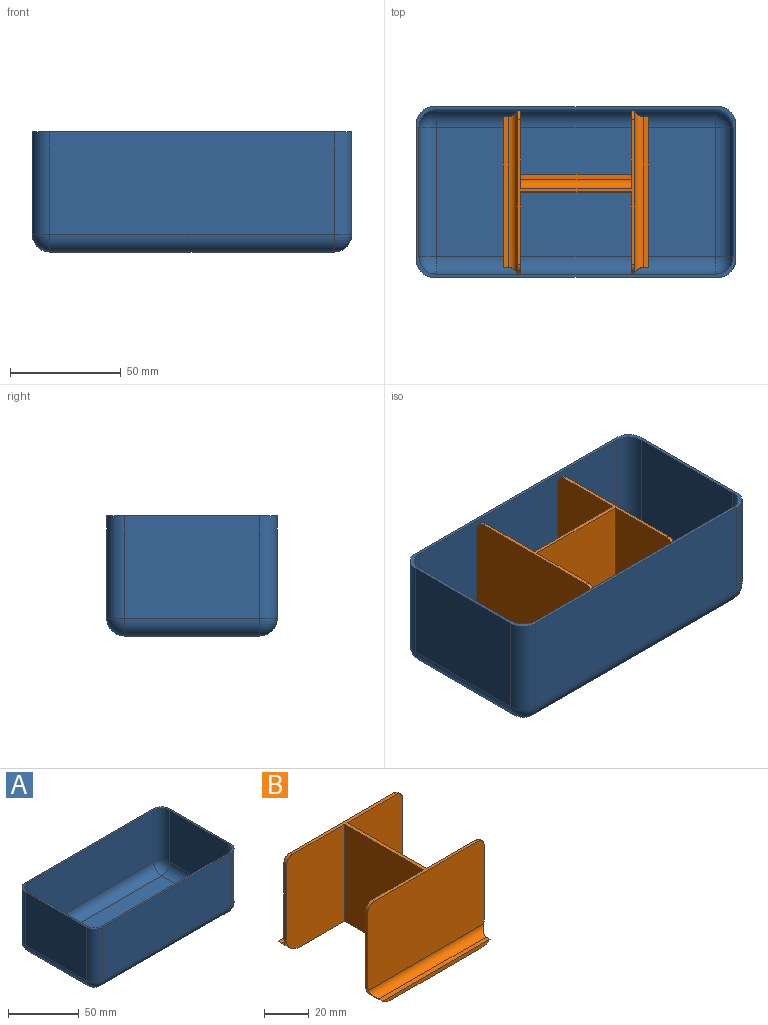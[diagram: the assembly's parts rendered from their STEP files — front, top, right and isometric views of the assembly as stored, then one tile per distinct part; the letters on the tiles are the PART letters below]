
ASSEMBLY  parts=2 mates=1
PART A: 35 faces, bbox 144.6x77.1x54.3 mm
  f0: plane 61.1x46.3mm, normal (1,0,0), area 2828.9mm2, adj f8,f13,f16,f26
  f1: plane 128.6x46.3mm, normal (0,1,0), area 5954.2mm2, adj f8,f13,f14,f22
  f2: plane 61.1x46.3mm, normal (-1,0,0), area 2828.9mm2, adj f8,f14,f15,f19
  f3: plane 58.5x45mm, normal (1,0,0), area 2632.5mm2, adj f8,f9,f12,f32
  f4: plane 126x45mm, normal (0,-1,0), area 5670mm2, adj f8,f9,f10,f28
  f5: plane 58.5x45mm, normal (-1,0,0), area 2632.5mm2, adj f8,f10,f11,f29
  f6: plane 126x45mm, normal (0,1,0), area 5670mm2, adj f8,f11,f12,f33
  f7: plane 128.6x46.3mm, normal (0,-1,0), area 5954.2mm2, adj f8,f15,f16,f23
  f8: plane 144.6x77.1mm, normal (0,0,1), area 569.7mm2, adj f0,f1,f2,f3,f4,f5,f6,f7
  f9: cylinder r=8mm len=45mm, axis (0,0,-1), area 565.5mm2, adj f3,f4,f8,f30
  f10: cylinder r=8mm len=45mm, axis (0,0,1), area 565.5mm2, adj f4,f5,f8,f27
  f11: cylinder r=8mm len=45mm, axis (0,0,-1), area 565.5mm2, adj f5,f6,f8,f31
  f12: cylinder r=8mm len=45mm, axis (0,0,1), area 565.5mm2, adj f3,f6,f8,f34
  f13: cylinder r=8mm len=46.3mm, axis (0,0,-1), area 581.8mm2, adj f0,f1,f8,f24
  f14: cylinder r=8mm len=46.3mm, axis (0,0,1), area 581.8mm2, adj f1,f2,f8,f20
  f15: cylinder r=8mm len=46.3mm, axis (0,0,-1), area 581.8mm2, adj f2,f7,f8,f21
  f16: cylinder r=8mm len=46.3mm, axis (0,0,1), area 581.8mm2, adj f0,f7,f8,f25
  f17: plane 126x58.5mm, normal (0,0,1), area 7371mm2, adj f28,f29,f32,f33
  f18: plane 128.6x61.1mm, normal (0,0,-1), area 7857.5mm2, adj f19,f22,f23,f26
  f19: cylinder r=8mm len=61.1mm, axis (0,-1,0), area 767.8mm2, adj f2,f18,f20,f21
  f20: sphere r=8mm, area 100.5mm2, adj f14,f19,f22
  f21: sphere r=8mm, area 100.5mm2, adj f15,f19,f23
  f22: cylinder r=8mm len=128.6mm, axis (-1,0,0), area 1616mm2, adj f1,f18,f20,f24
  f23: cylinder r=8mm len=128.6mm, axis (1,0,0), area 1616mm2, adj f7,f18,f21,f25
  f24: sphere r=8mm, area 100.5mm2, adj f13,f22,f26
  f25: sphere r=8mm, area 100.5mm2, adj f16,f23,f26
  f26: cylinder r=8mm len=61.1mm, axis (0,1,0), area 767.8mm2, adj f0,f18,f24,f25
  f27: sphere r=8mm, area 100.5mm2, adj f10,f28,f29
  f28: cylinder r=8mm len=126mm, axis (1,0,0), area 1583.4mm2, adj f4,f17,f27,f30
  f29: cylinder r=8mm len=58.5mm, axis (0,-1,0), area 735.1mm2, adj f5,f17,f27,f31
  f30: sphere r=8mm, area 100.5mm2, adj f9,f28,f32
  f31: sphere r=8mm, area 100.5mm2, adj f11,f29,f33
  f32: cylinder r=8mm len=58.5mm, axis (0,1,0), area 735.1mm2, adj f3,f17,f30,f34
  f33: cylinder r=8mm len=126mm, axis (-1,0,0), area 1583.4mm2, adj f6,f17,f31,f34
  f34: sphere r=8mm, area 100.5mm2, adj f12,f32,f33
PART B: 31 faces, bbox 73.5x66x53 mm
  f0: plane 66x57.5mm, normal (0,0,-1), area 1320mm2, adj f1,f5,f6,f7,f10,f13,f14,f17
  f1: plane 50x2mm, normal (1,0,0), area 100mm2, adj f0,f2,f10,f13
  f2: plane 50x2.4mm, normal (0,0,1), area 120mm2, adj f1,f10,f13,f26
  f3: plane 50x47mm, normal (1,0,0), area 2350mm2, adj f4,f10,f13,f26
  f4: plane 65.5x53.2mm, normal (0,0,1), area 289.6mm2, adj f3,f5,f6,f9,f10,f13,f14,f15
  f5: plane 53x50mm, normal (-1,0,0), area 2650mm2, adj f0,f4,f6,f14
  f6: plane 53x36.75mm, normal (0,-1,0), area 1930.6mm2, adj f0,f4,f5,f12,f22,f29
  f7: plane 68.08x2mm, normal (0,1,0), area 129.5mm2, adj f0,f8,f22,f23
  f8: plane 68.08x2.4mm, normal (0,0,1), area 163.4mm2, adj f7,f22,f23,f24
  f9: plane 73.5x47mm, normal (0,1,0), area 3447.3mm2, adj f4,f11,f12,f22,f23,f24,f29,f30
  f10: plane 53x35.15mm, normal (0,-1,0), area 1829.5mm2, adj f0,f1,f2,f3,f4,f11,f23,f26
  f11: plane 41x1.6mm, normal (1,0,0), area 65.6mm2, adj f9,f10,f23,f30
  f12: plane 41x1.6mm, normal (-1,0,0), area 65.6mm2, adj f6,f9,f22,f29
  f13: plane 53x35.15mm, normal (0,1,0), area 1829.5mm2, adj f0,f1,f2,f3,f4,f18,f21,f26
  f14: plane 53x36.75mm, normal (0,1,0), area 1930.6mm2, adj f0,f4,f5,f19,f20,f27
  f15: plane 73.5x47mm, normal (0,-1,0), area 3447.3mm2, adj f4,f18,f19,f20,f21,f25,f27,f28
  f16: plane 68.08x2.4mm, normal (0,0,1), area 163.4mm2, adj f17,f20,f21,f25
  f17: plane 68.08x2mm, normal (0,-1,0), area 129.5mm2, adj f0,f16,f20,f21
  f18: plane 41x1.6mm, normal (1,0,0), area 65.6mm2, adj f13,f15,f21,f28
  f19: plane 41x1.6mm, normal (-1,0,0), area 65.6mm2, adj f14,f15,f20,f27
  f20: cylinder r=8mm len=8mm, axis (0,1,0), area 61.7mm2, adj f0,f14,f15,f16,f17,f19,f25
  f21: cylinder r=8mm len=8mm, axis (0,-1,0), area 61.7mm2, adj f0,f13,f15,f16,f17,f18,f25
  f22: cylinder r=8mm len=8mm, axis (0,1,0), area 61.7mm2, adj f0,f6,f7,f8,f9,f12,f24
  f23: cylinder r=8mm len=8mm, axis (0,-1,0), area 61.7mm2, adj f0,f7,f8,f9,f10,f11,f24
  f24: cylinder r=4mm len=72.99mm, axis (-1,0,0), area 441.9mm2, adj f8,f9,f22,f23
  f25: cylinder r=4mm len=72.99mm, axis (1,0,0), area 441.9mm2, adj f15,f16,f20,f21
  f26: cylinder r=4mm len=50mm, axis (0,1,0), area 314.2mm2, adj f2,f3,f10,f13
  f27: cylinder r=4mm len=4mm, axis (0,-1,0), area 10.1mm2, adj f4,f14,f15,f19
  f28: cylinder r=4mm len=4mm, axis (0,1,0), area 10.1mm2, adj f4,f13,f15,f18
  f29: cylinder r=4mm len=4mm, axis (0,-1,0), area 10.1mm2, adj f4,f6,f9,f12
  f30: cylinder r=4mm len=4mm, axis (0,1,0), area 10.1mm2, adj f4,f9,f10,f11
PLACE A t=(-46.38,-20.9,-6.43)mm
PLACE B rot(axis=(0,0,1),90deg) t=(-46.38,-20.9,-6.43)mm
MATE revolute B.f0 <-> A.f17  axis (0,0,1) through (-46.38,-20.9,-6.43)mm
